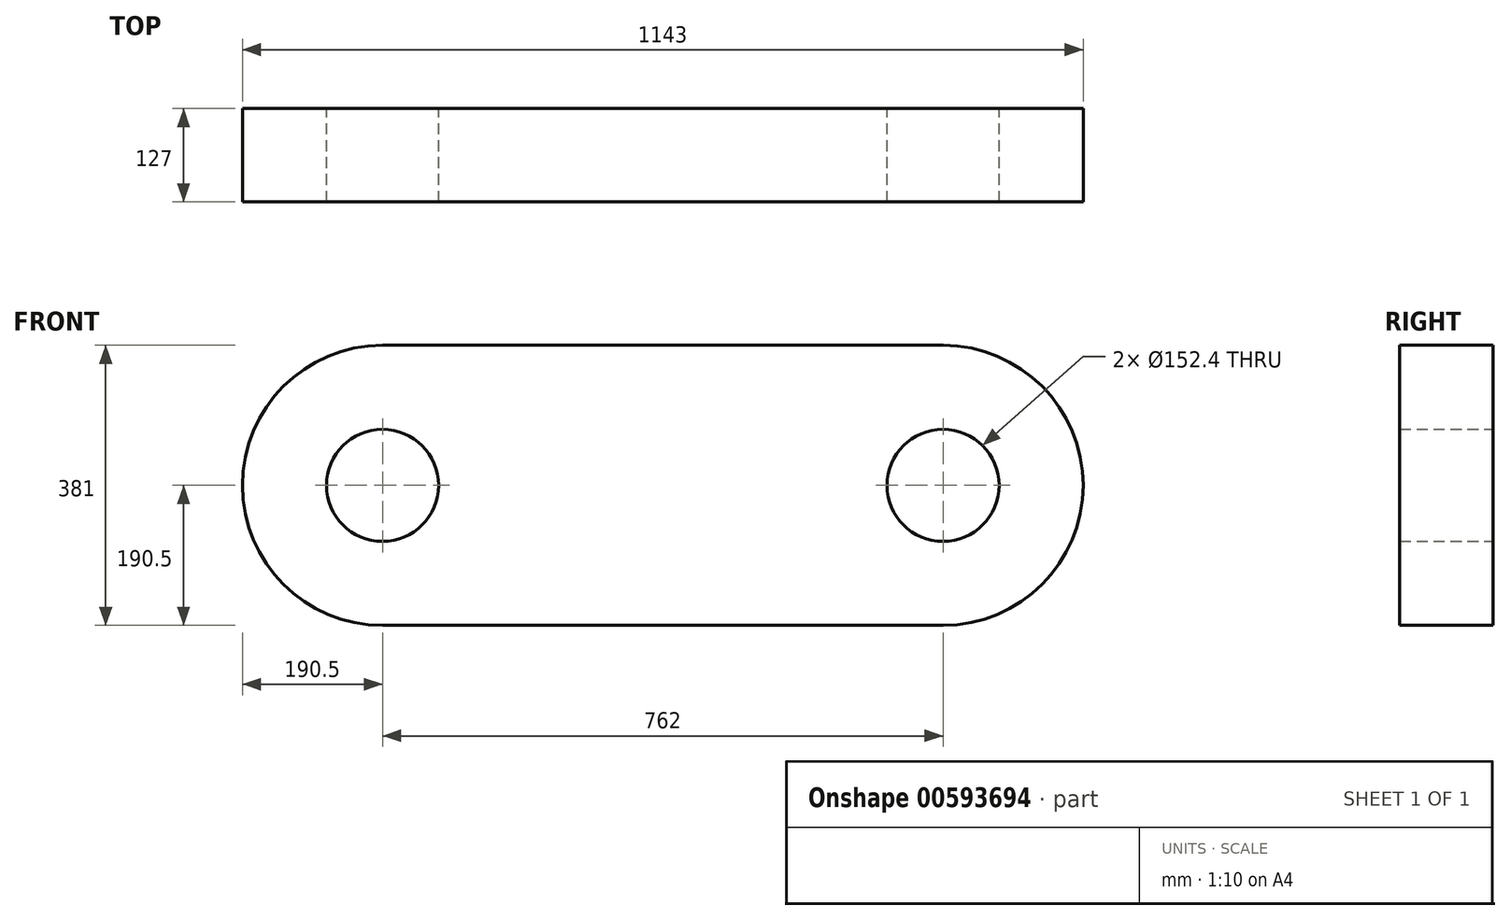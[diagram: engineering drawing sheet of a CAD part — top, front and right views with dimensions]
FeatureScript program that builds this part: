
annotation { "Feature Type Name" : "Feature", "Feature Type Description" : "" }
export const myFeature = defineFeature(function(context is Context, id is Id, definition is map)
    precondition{}
    {
        {
            var Q0;
            Q0=qCreatedBy(makeId("Front.planeOp"),FACE);
            var sketch = newSketch(context, id + "F0", { "sketchPlane" : qUnion([Q0])});
            skLineSegment(sketch, "E0.bottom", {"start": v(-381, 190.5) * mm, "end": v(381, 190.5) * mm});
            skLineSegment(sketch, "E0.top", {"start": v(-381, -190.5) * mm, "end": v(381, -190.5) * mm});
            skLineSegment(sketch, "E0.left", {"start": v(-381, 190.5) * mm, "end": v(-381, -190.5) * mm, "construction": true});
            skLineSegment(sketch, "E0.right", {"start": v(381, 190.5) * mm, "end": v(381, -190.5) * mm, "construction": true});
            skArc(sketch, "E1", {"start": v(-381, 190.5) * mm, "mid": v(-571.5, 0) * mm, "end": v(-381, -190.5) * mm});
            skArc(sketch, "E2.MirrorCS", {"start": v(381, 190.5) * mm, "mid": v(571.5, 0) * mm, "end": v(381, -190.5) * mm});
            skCircle(sketch, "E3", {"center": v(-381, 0) * mm, "radius": 76.2 * mm});
            skCircle(sketch, "E4", {"center": v(381, 0) * mm, "radius": 76.2 * mm});
            skSolve(sketch);
        }
        {
            var Q0;
            Q0 = qSketchRegion(id + "F0", true);
            extrude(context, id + "F1", {"entities" : qUnion([Q0]), "depth" : 127 * mm, "offsetDistance" : 25.4 * mm});
        }
    });
